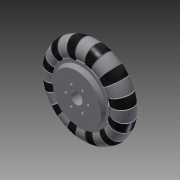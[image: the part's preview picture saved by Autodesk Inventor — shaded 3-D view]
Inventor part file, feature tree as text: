
AUTODESK INVENTOR PART (.ipt)
format: ipt  version: 2015 (Build 190159000, 159)  size: 737,792 bytes
history: native  units: in
note: dims shown in document units (in); Inventor stores cm internally (conversion verified against a paired STEP export)
features: sketch x10, revolve x6, plane x4, pattern_circular x3, extrude x2
ambient origin geometry x8: Origin, YZ Plane, XZ Plane, XY Plane, X Axis, Y Axis, Z Axis, Center Point
bodies: Solid1 (feature_tree)
feature tree (25):
  revolve  "Revolution1"  [1 undecoded]
  revolve  "Revolution2"  [1 undecoded]
  pattern_circular  "Circular Pattern1"  Count=12 Angle=360.0deg
  sketch  "Sketch3"  dims[d7=0.0039in]
  revolve  "Revolution3"  [1 undecoded]
  sketch  "Sketch5"  dims[d9=0.0157in]
  plane  "Work Plane2"
  plane  "Work Plane6"
  revolve  "Revolution4"  Angle=360.0deg
  plane  "Work Plane4"
  revolve  "Revolution5"  [1 undecoded]
  pattern_circular  "Circular Pattern2"  [2 undecoded]
  plane  "Work Plane5"
  revolve  "Revolution6"  [1 undecoded]
  extrude  "Extrusion1"  Depth=0.3937in
  extrude  "Extrusion2"  Depth=0.3937in
  pattern_circular  "Circular Pattern3"  [2 undecoded]
  sketch  "Sketch1"  dims[d0=0.0984in d2=0.0197in]
  sketch  "Sketch2"  dims[d5=0.0079in d6=0.0079in]
  sketch  "Sketch4"  dims[d8=90.0deg]
  sketch  "Sketch7"  dims[d10=0.0315in]
  sketch  "Sketch9"  dims[d11=15.0deg d12=4.7244in d13=360.0deg]
  sketch  "Sketch10"  dims[d15=15.0deg d17=0.0962in]
  sketch  "Sketch11"  dims[d18=0.0893in d19=4.7244in d20=360.0deg]
  sketch  "Sketch12"  dims[d22=0.0079in d23=0.0893in d24=0.0295in d25=0.0276in d26=0.0354in d27=0.0315in d28=0.3937in d29=0.0in d30=0.0276in d31=0.0079in d32=0.3937in d33=0.0in d34=2.3622in d35=360.0deg]
note: 9 required parameter values undecoded (feature->parameter linkage not recoverable at this tier; creation-order binding heuristic only, values carry confidence <= 0.55)